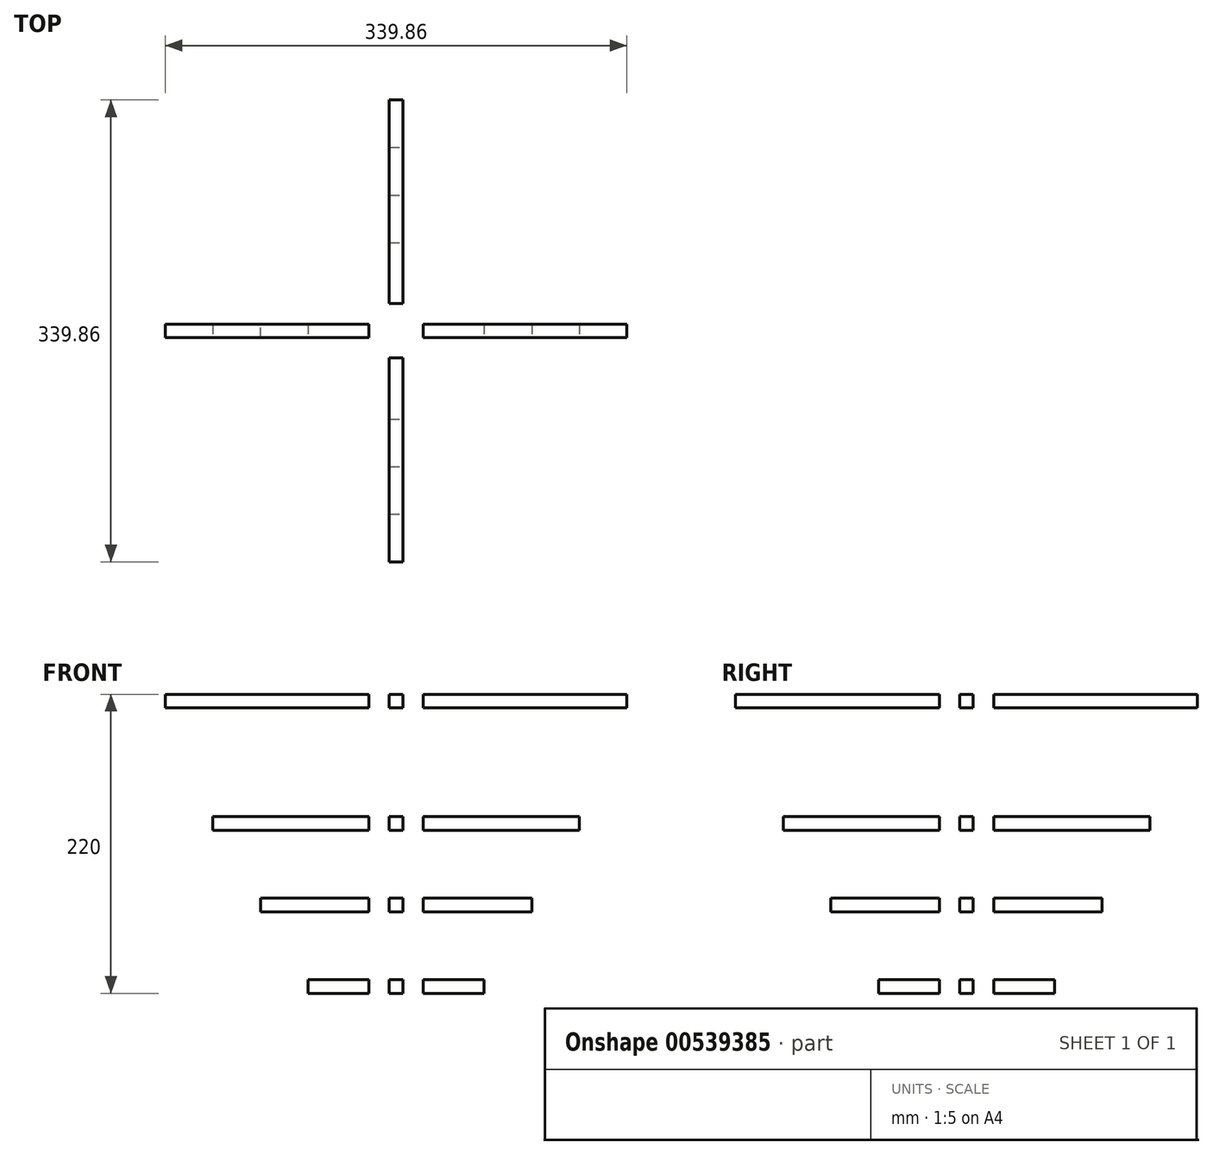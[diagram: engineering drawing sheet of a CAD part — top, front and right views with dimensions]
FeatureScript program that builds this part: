
annotation { "Feature Type Name" : "Feature", "Feature Type Description" : "" }
export const myFeature = defineFeature(function(context is Context, id is Id, definition is map)
    precondition{}
    {
        {
            var Q0;
            Q0=qCreatedBy(makeId("Top.planeOp"),FACE);
            var sketch = newSketch(context, id + "F0", { "sketchPlane" : qUnion([Q0])});
            skCircle(sketch, "E0", {"center": v(0, 0) * mm, "radius": 170 * mm});
            skSolve(sketch);
        }
        {
            var Q0;
            Q0=makeQuery(id+"F0.imprint","IMPRINT",FACE,{"disambiguationData":[TD([[makeQuery(id+"F0.imprint","IMPRINT",EDGE,{"derivedFrom":sQuery(id+"F0.wireOp",EDGE,"E0")}),1.0]])]});
            var Q1;
            Q1=sQuery(id+"F0.wireOp",EDGE,"E0");
            extrude(context, id + "F1", {"entities" : qUnion([Q0]), "bodyType" : ToolBodyType.SURFACE, "surfaceEntities" : qUnion([Q1]), "oppositeDirection" : true, "depth" : 15 * mm, "offsetDistance" : 25 * mm});
        }
        {
            var Q0;
            Q0=qCreatedBy(makeId("Top.planeOp"),FACE);
            cPlane(context, id + "F2", {"entities" : qUnion([Q0]), "cplaneType" : CPlaneType.OFFSET, "offset" : 90 * mm, "oppositeDirection" : true, "width" : 150 * mm, "height" : 150 * mm});
        }
        {
            var Q0;
            Q0=qCreatedBy(id+"F2.planeOp",FACE);
            var sketch = newSketch(context, id + "F3", { "sketchPlane" : qUnion([Q0])});
            skCircle(sketch, "E1", {"center": v(0, 0) * mm, "radius": 135 * mm});
            skSolve(sketch);
        }
        {
            var Q0;
            Q0=sQuery(id+"F3.wireOp",EDGE,"E1");
            extrude(context, id + "F4", {"bodyType" : ToolBodyType.SURFACE, "surfaceEntities" : qUnion([Q0]), "oppositeDirection" : true, "depth" : 15 * mm, "offsetDistance" : 25 * mm});
        }
        {
            var Q0;
            Q0=qCreatedBy(id+"F2.planeOp",FACE);
            cPlane(context, id + "F5", {"entities" : qUnion([Q0]), "cplaneType" : CPlaneType.OFFSET, "offset" : 60 * mm, "oppositeDirection" : true, "width" : 150 * mm, "height" : 150 * mm});
        }
        {
            var Q0;
            Q0=qCreatedBy(id+"F5.planeOp",FACE);
            var sketch = newSketch(context, id + "F6", { "sketchPlane" : qUnion([Q0])});
            skCircle(sketch, "E2", {"center": v(0, 0) * mm, "radius": 100 * mm});
            skSolve(sketch);
        }
        {
            var Q0;
            Q0 = qSketchRegion(id + "F6", true);
            var Q1;
            Q1=sQuery(id+"F6.wireOp",EDGE,"E2");
            extrude(context, id + "F7", {"entities" : qUnion([Q0]), "bodyType" : ToolBodyType.SURFACE, "surfaceEntities" : qUnion([Q1]), "oppositeDirection" : true, "depth" : 15 * mm, "offsetDistance" : 25 * mm});
        }
        {
            var Q0;
            Q0=qCreatedBy(id+"F5.planeOp",FACE);
            cPlane(context, id + "F8", {"entities" : qUnion([Q0]), "cplaneType" : CPlaneType.OFFSET, "offset" : 60 * mm, "oppositeDirection" : true, "width" : 150 * mm, "height" : 150 * mm});
        }
        {
            var Q0;
            Q0=qCreatedBy(id+"F8.planeOp",FACE);
            var sketch = newSketch(context, id + "F9", { "sketchPlane" : qUnion([Q0])});
            skCircle(sketch, "E3", {"center": v(0, 0) * mm, "radius": 65 * mm});
            skSolve(sketch);
        }
        {
            var Q0;
            Q0 = qSketchRegion(id + "F9", true);
            var Q1;
            Q1=sQuery(id+"F9.wireOp",EDGE,"E3");
            extrude(context, id + "F10", {"entities" : qUnion([Q0]), "bodyType" : ToolBodyType.SURFACE, "surfaceEntities" : qUnion([Q1]), "oppositeDirection" : true, "depth" : 15 * mm, "offsetDistance" : 25 * mm});
        }
        {
            var Q0;
            Q0=qCreatedBy(id+"F8.planeOp",FACE);
            cPlane(context, id + "F11", {"entities" : qUnion([Q0]), "cplaneType" : CPlaneType.OFFSET, "offset" : 60 * mm, "oppositeDirection" : true, "width" : 150 * mm, "height" : 150 * mm});
        }
        {
            var Q0;
            Q0=qCreatedBy(id+"F11.planeOp",FACE);
            var sketch = newSketch(context, id + "F12", { "sketchPlane" : qUnion([Q0])});
            skCircle(sketch, "E4", {"center": v(0, 0) * mm, "radius": 30 * mm});
            skSolve(sketch);
        }
        {
            var Q0;
            Q0 = qSketchRegion(id + "F12", true);
            var Q1;
            Q1=sQuery(id+"F12.wireOp",EDGE,"E4");
            extrude(context, id + "F13", {"entities" : qUnion([Q0]), "bodyType" : ToolBodyType.SURFACE, "surfaceEntities" : qUnion([Q1]), "oppositeDirection" : true, "depth" : 15 * mm, "offsetDistance" : 25 * mm});
        }
        {
            var Q0;
            Q0=qCreatedBy(makeId("Top.planeOp"),FACE);
            var sketch = newSketch(context, id + "F14", { "sketchPlane" : qUnion([Q0])});
            skLineSegment(sketch, "E5.bottom", {"start": v(-20, -20) * mm, "end": v(20, -20) * mm});
            skLineSegment(sketch, "E5.top", {"start": v(-20, 20) * mm, "end": v(20, 20) * mm});
            skLineSegment(sketch, "E5.left", {"start": v(-20, -20) * mm, "end": v(-20, 20) * mm});
            skLineSegment(sketch, "E5.right", {"start": v(20, -20) * mm, "end": v(20, 20) * mm});
            skSolve(sketch);
        }
        {
            var Q0;
            Q0 = qSketchRegion(id + "F14", true);
            var Q1;
            Q1=sQuery(id+"F14.wireOp",EDGE,"E5.left");
            var Q2;
            Q2=sQuery(id+"F14.wireOp",EDGE,"E5.right");
            var Q3;
            Q3=sQuery(id+"F14.wireOp",EDGE,"E5.bottom");
            var Q4;
            Q4=sQuery(id+"F14.wireOp",EDGE,"E5.top");
            extrude(context, id + "F15", {"entities" : qUnion([Q0]), "bodyType" : ToolBodyType.SURFACE, "surfaceEntities" : qUnion([Q1, Q2, Q3, Q4]), "oppositeDirection" : true, "depth" : 280 * mm, "offsetDistance" : 25 * mm});
        }
        {
            var Q0;
            Q0=qCreatedBy(makeId("Top.planeOp"),FACE);
            var sketch = newSketch(context, id + "F16", { "sketchPlane" : qUnion([Q0])});
            skLineSegment(sketch, "E6.bottom", {"start": v(-20, 5) * mm, "end": v(-169.93, 5) * mm});
            skLineSegment(sketch, "E6.top", {"start": v(-20, -5) * mm, "end": v(-169.93, -5) * mm});
            skLineSegment(sketch, "E6.left", {"start": v(-20, 5) * mm, "end": v(-20, -5) * mm});
            skLineSegment(sketch, "E6.right", {"start": v(-169.93, 5) * mm, "end": v(-169.93, -5) * mm});
            skLineSegment(sketch, "E7.bottom", {"start": v(20, 5) * mm, "end": v(169.93, 5) * mm});
            skLineSegment(sketch, "E7.top", {"start": v(20, -5) * mm, "end": v(169.93, -5) * mm});
            skLineSegment(sketch, "E7.left", {"start": v(20, 5) * mm, "end": v(20, -5) * mm});
            skLineSegment(sketch, "E7.right", {"start": v(169.93, 5) * mm, "end": v(169.93, -5) * mm});
            skLineSegment(sketch, "E8.bottom", {"start": v(-5, 20) * mm, "end": v(5, 20) * mm});
            skLineSegment(sketch, "E8.top", {"start": v(-5, 169.93) * mm, "end": v(5, 169.93) * mm});
            skLineSegment(sketch, "E8.left", {"start": v(-5, 20) * mm, "end": v(-5, 169.93) * mm});
            skLineSegment(sketch, "E8.right", {"start": v(5, 20) * mm, "end": v(5, 169.93) * mm});
            skLineSegment(sketch, "E9.bottom", {"start": v(-5, -20) * mm, "end": v(5, -20) * mm});
            skLineSegment(sketch, "E9.top", {"start": v(-5, -169.93) * mm, "end": v(5, -169.93) * mm});
            skLineSegment(sketch, "E9.left", {"start": v(-5, -20) * mm, "end": v(-5, -169.93) * mm});
            skLineSegment(sketch, "E9.right", {"start": v(5, -20) * mm, "end": v(5, -169.93) * mm});
            skSolve(sketch);
        }
        {
            var Q0;
            Q0 = qSketchRegion(id + "F16", true);
            extrude(context, id + "F17", {"entities" : qUnion([Q0]), "oppositeDirection" : true, "depth" : 10 * mm, "offsetDistance" : 25 * mm});
        }
        {
            var Q0;
            Q0=qCreatedBy(id+"F2.planeOp",FACE);
            var sketch = newSketch(context, id + "F18", { "sketchPlane" : qUnion([Q0])});
            skLineSegment(sketch, "E10.bottom", {"start": v(-20, 5) * mm, "end": v(-134.9, 5) * mm});
            skLineSegment(sketch, "E10.top", {"start": v(-20, -5) * mm, "end": v(-134.9, -5) * mm});
            skLineSegment(sketch, "E10.left", {"start": v(-20, 5) * mm, "end": v(-20, -5) * mm});
            skLineSegment(sketch, "E10.right", {"start": v(-134.9, 5) * mm, "end": v(-134.9, -5) * mm});
            skLineSegment(sketch, "E11.bottom", {"start": v(20, 5) * mm, "end": v(134.9, 5) * mm});
            skLineSegment(sketch, "E11.top", {"start": v(20, -5) * mm, "end": v(134.9, -5) * mm});
            skLineSegment(sketch, "E11.left", {"start": v(20, 5) * mm, "end": v(20, -5) * mm});
            skLineSegment(sketch, "E11.right", {"start": v(134.9, 5) * mm, "end": v(134.9, -5) * mm});
            skLineSegment(sketch, "E12.bottom", {"start": v(-5, -20) * mm, "end": v(5, -20) * mm});
            skLineSegment(sketch, "E12.top", {"start": v(-5, -134.9) * mm, "end": v(5, -134.9) * mm});
            skLineSegment(sketch, "E12.left", {"start": v(-5, -20) * mm, "end": v(-5, -134.9) * mm});
            skLineSegment(sketch, "E12.right", {"start": v(5, -20) * mm, "end": v(5, -134.9) * mm});
            skPoint(sketch, "E13.top.end.orphan", {"position": v(0, 144.26) * mm});
            skLineSegment(sketch, "E14.bottom", {"start": v(-5, 20) * mm, "end": v(5, 20) * mm});
            skLineSegment(sketch, "E14.top", {"start": v(-5, 134.9) * mm, "end": v(5, 134.9) * mm});
            skLineSegment(sketch, "E14.left", {"start": v(-5, 20) * mm, "end": v(-5, 134.9) * mm});
            skLineSegment(sketch, "E14.right", {"start": v(5, 20) * mm, "end": v(5, 134.9) * mm});
            skSolve(sketch);
        }
        {
            var Q0;
            Q0 = qSketchRegion(id + "F18", true);
            extrude(context, id + "F19", {"entities" : qUnion([Q0]), "oppositeDirection" : true, "depth" : 10 * mm, "offsetDistance" : 25 * mm});
        }
        {
            var Q0;
            Q0=qCreatedBy(id+"F5.planeOp",FACE);
            var sketch = newSketch(context, id + "F20", { "sketchPlane" : qUnion([Q0])});
            skLineSegment(sketch, "E15.bottom", {"start": v(-99.87, -5) * mm, "end": v(-20, -5) * mm});
            skLineSegment(sketch, "E15.top", {"start": v(-99.87, 5) * mm, "end": v(-20, 5) * mm});
            skLineSegment(sketch, "E15.left", {"start": v(-99.87, -5) * mm, "end": v(-99.87, 5) * mm});
            skLineSegment(sketch, "E15.right", {"start": v(-20, -5) * mm, "end": v(-20, 5) * mm});
            skLineSegment(sketch, "E16.bottom", {"start": v(-5, 20) * mm, "end": v(5, 20) * mm});
            skLineSegment(sketch, "E16.top", {"start": v(-5, 99.87) * mm, "end": v(5, 99.87) * mm});
            skLineSegment(sketch, "E16.left", {"start": v(-5, 20) * mm, "end": v(-5, 99.87) * mm});
            skLineSegment(sketch, "E16.right", {"start": v(5, 20) * mm, "end": v(5, 99.87) * mm});
            skLineSegment(sketch, "E17.bottom", {"start": v(20, 5) * mm, "end": v(99.87, 5) * mm});
            skLineSegment(sketch, "E17.top", {"start": v(20, -5) * mm, "end": v(99.87, -5) * mm});
            skLineSegment(sketch, "E17.left", {"start": v(20, 5) * mm, "end": v(20, -5) * mm});
            skLineSegment(sketch, "E17.right", {"start": v(99.87, 5) * mm, "end": v(99.87, -5) * mm});
            skLineSegment(sketch, "E18.bottom", {"start": v(-5, -20) * mm, "end": v(5, -20) * mm});
            skLineSegment(sketch, "E18.top", {"start": v(-5, -99.87) * mm, "end": v(5, -99.87) * mm});
            skLineSegment(sketch, "E18.left", {"start": v(-5, -20) * mm, "end": v(-5, -99.87) * mm});
            skLineSegment(sketch, "E18.right", {"start": v(5, -20) * mm, "end": v(5, -99.87) * mm});
            skSolve(sketch);
        }
        {
            var Q0;
            Q0 = qSketchRegion(id + "F20", true);
            extrude(context, id + "F21", {"entities" : qUnion([Q0]), "oppositeDirection" : true, "depth" : 10 * mm, "offsetDistance" : 25 * mm});
        }
        {
            var Q0;
            Q0=qCreatedBy(id+"F8.planeOp",FACE);
            var sketch = newSketch(context, id + "F22", { "sketchPlane" : qUnion([Q0])});
            skLineSegment(sketch, "E19.bottom", {"start": v(-20, 5) * mm, "end": v(-64.8, 5) * mm});
            skLineSegment(sketch, "E19.top", {"start": v(-20, -5) * mm, "end": v(-64.8, -5) * mm});
            skLineSegment(sketch, "E19.left", {"start": v(-20, 5) * mm, "end": v(-20, -5) * mm});
            skLineSegment(sketch, "E19.right", {"start": v(-64.8, 5) * mm, "end": v(-64.8, -5) * mm});
            skLineSegment(sketch, "E20.bottom", {"start": v(-5, -20) * mm, "end": v(5, -20) * mm});
            skLineSegment(sketch, "E20.top", {"start": v(-5, -64.8) * mm, "end": v(5, -64.8) * mm});
            skLineSegment(sketch, "E20.left", {"start": v(-5, -20) * mm, "end": v(-5, -64.8) * mm});
            skLineSegment(sketch, "E20.right", {"start": v(5, -20) * mm, "end": v(5, -64.8) * mm});
            skLineSegment(sketch, "E21.bottom", {"start": v(20, 5) * mm, "end": v(64.8, 5) * mm});
            skLineSegment(sketch, "E21.top", {"start": v(20, -5) * mm, "end": v(64.8, -5) * mm});
            skLineSegment(sketch, "E21.left", {"start": v(20, 5) * mm, "end": v(20, -5) * mm});
            skLineSegment(sketch, "E21.right", {"start": v(64.8, 5) * mm, "end": v(64.8, -5) * mm});
            skLineSegment(sketch, "E22.bottom", {"start": v(-5, 20) * mm, "end": v(5, 20) * mm});
            skLineSegment(sketch, "E22.top", {"start": v(-5, 64.8) * mm, "end": v(5, 64.8) * mm});
            skLineSegment(sketch, "E22.left", {"start": v(-5, 20) * mm, "end": v(-5, 64.8) * mm});
            skLineSegment(sketch, "E22.right", {"start": v(5, 20) * mm, "end": v(5, 64.8) * mm});
            skSolve(sketch);
        }
        {
            var Q0;
            Q0 = qSketchRegion(id + "F22", true);
            extrude(context, id + "F23", {"entities" : qUnion([Q0]), "oppositeDirection" : true, "depth" : 10 * mm, "offsetDistance" : 25 * mm});
        }
    });
